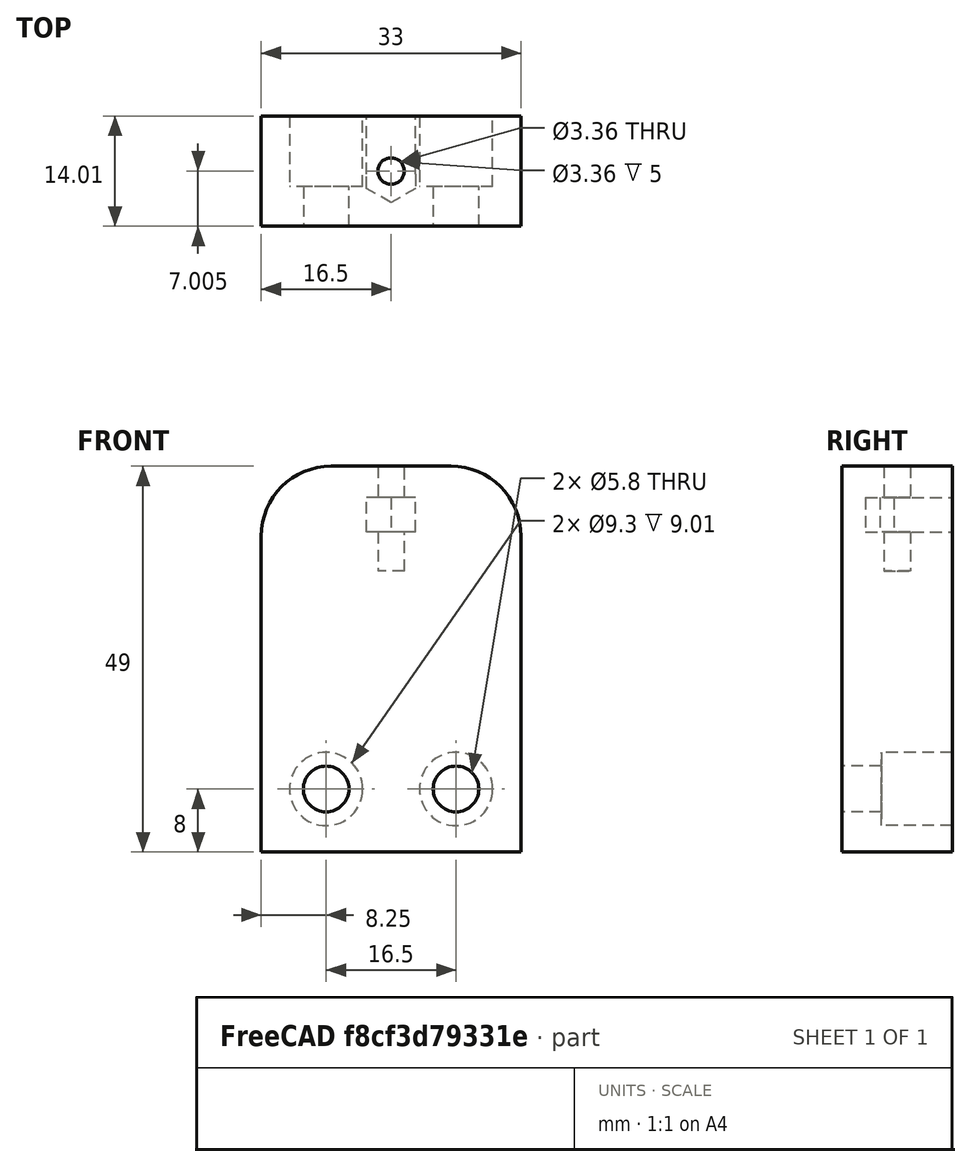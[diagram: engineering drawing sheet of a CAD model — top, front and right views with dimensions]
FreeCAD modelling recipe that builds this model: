
FCSTD DOCUMENT  (FreeCAD 0.16R6706 (Git))
Label: idler_pulley_holder_31_above_h
License: All rights reserved
LicenseURL: http://en.wikipedia.org/wiki/All_rights_reserved
objects: Part::Feature×1, Part::Fillet×1, Part::Prism×1, Part::Box×1, Part::Fuse×1, Part::Cut×1
note: 6 computed .brp shape members not serialized (recipe doc carries the construction recipe); baked Part::Feature solids carry a one-line shape summary decoded from their .brp

FEATURE [Part::Feature] idlepulleyhold_aux
  shape: bbox 33 x 14.01 x 49 mm, 14 faces (baked)
FEATURE [Part::Fillet] idlepulleyhold_chmf
  Base = -> idlepulleyhold_aux
  Edges = 2 edges r=8.895: [Edge9,Edge12]
FEATURE [Part::Prism] idlepulleyhold_nuthole_nut
  Circumradius = 3.605
  Height = 4.32
  Placement = pos=(0,0,0) rot=(-0.57735,0.57735,0.57735;2.0944rad)
  Polygon = 6
FEATURE [Part::Box] idlepulleyhold_nuthole_hole
  Height = 8.405
  Length = 6.24408
  Placement = pos=(-3.12204,0,0) rot=(0,0,1;0rad)
  Width = 4.32
FEATURE [Part::Fuse] idlepulleyhold_nuthole
  Base = -> idlepulleyhold_nuthole_nut
  Placement = pos=(0,6.605,27) rot=(-1,0,0;1.5708rad)
  Tool = -> idlepulleyhold_nuthole_hole
FEATURE [Part::Cut] idlepulleyhold
  Base = -> idlepulleyhold_chmf
  Tool = -> idlepulleyhold_nuthole
